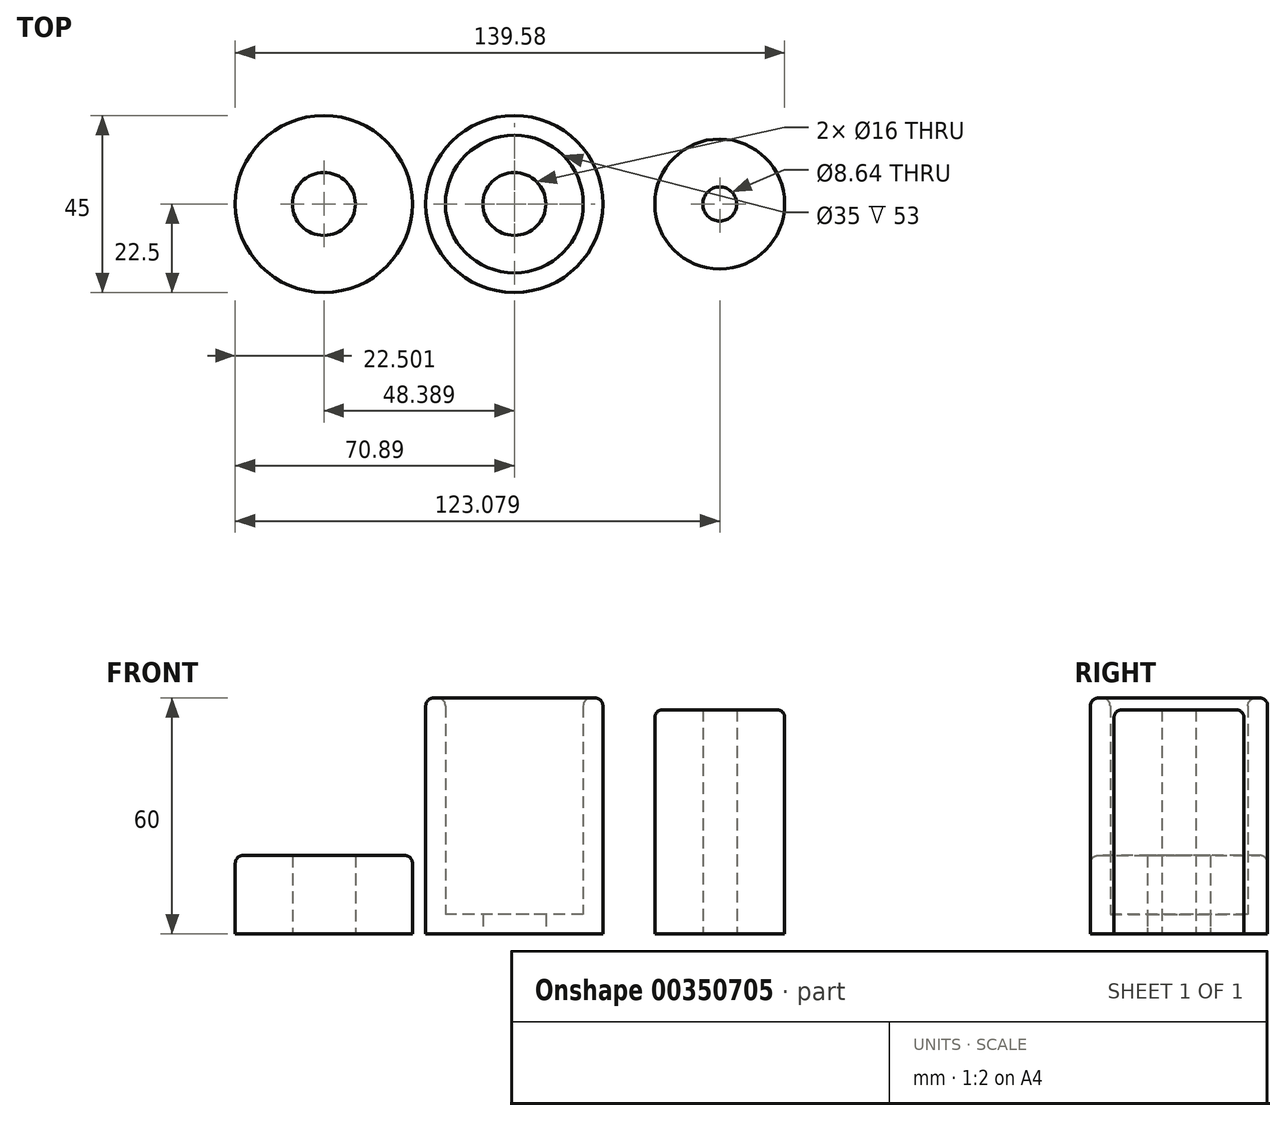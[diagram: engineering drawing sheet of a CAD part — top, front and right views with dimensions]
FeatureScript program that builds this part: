
annotation { "Feature Type Name" : "Feature", "Feature Type Description" : "" }
export const myFeature = defineFeature(function(context is Context, id is Id, definition is map)
    precondition{}
    {
        {
            var Q0;
            Q0=qCreatedBy(makeId("Top.planeOp"),FACE);
            var sketch = newSketch(context, id + "F0", { "sketchPlane" : qUnion([Q0])});
            skCircle(sketch, "E0", {"center": v(0, 0) * mm, "radius": 22.5 * mm});
            skSolve(sketch);
        }
        {
            var Q0;
            Q0 = qSketchRegion(id + "F0", true);
            extrude(context, id + "F1", {"entities" : qUnion([Q0]), "depth" : 60 * mm});
        }
        {
            var Q0;
            Q0=makeQuery(id+"F1.opExtrude","CAP_FACE",FACE,{"disambiguationData":[OSD([sQuery(id+"F0.wireOp",EDGE,"E0")])],"isStart":false});
            shell(context, id + "F2", {"entities" : qUnion([Q0]), "thickness" : 5 * mm});
        }
        {
            var Q0;
            Q0=qCreatedBy(makeId("Top.planeOp"),FACE);
            var sketch = newSketch(context, id + "F3", { "sketchPlane" : qUnion([Q0])});
            skCircle(sketch, "E1", {"center": v(52.19, 0) * mm, "radius": 16.5 * mm});
            skSolve(sketch);
        }
        {
            var Q0;
            Q0=makeQuery(id+"F3.imprint","IMPRINT",FACE,{"disambiguationData":[TD([[makeQuery(id+"F3.imprint","IMPRINT",EDGE,{"derivedFrom":sQuery(id+"F3.wireOp",EDGE,"E1")}),1.0]])]});
            extrude(context, id + "F4", {"entities" : qUnion([Q0]), "depth" : 57 * mm});
        }
        {
            var Q0;
            Q0=qCreatedBy(makeId("Top.planeOp"),FACE);
            var sketch = newSketch(context, id + "F5", { "sketchPlane" : qUnion([Q0])});
            skCircle(sketch, "E2", {"center": v(-48.39, 0) * mm, "radius": 22.5 * mm});
            skSolve(sketch);
        }
        {
            var Q0;
            Q0 = qSketchRegion(id + "F5", true);
            extrude(context, id + "F6", {"entities" : qUnion([Q0]), "depth" : 20 * mm});
        }
        {
            var Q0;
            Q0=makeQuery(id+"F4.opExtrude","CAP_EDGE",EDGE,{"disambiguationData":[OSD([sQuery(id+"F3.wireOp",EDGE,"E1")])],"isStart":false});
            var Q1;
            {var subQ0=sQuery(id+"F0.wireOp",EDGE,"E0");Q1=makeQuery(id+"F2.opShell","OFFSET_EDGE",EDGE,{"disambiguationData":[OSD([subQ0]),TDD([makeQuery(id+"F1.opExtrude","CAP_EDGE",EDGE,{"disambiguationData":[OSD([subQ0])],"isStart":false})])]});}
            var Q2;
            Q2=makeQuery(id+"F6.opExtrude","CAP_EDGE",EDGE,{"disambiguationData":[OSD([sQuery(id+"F5.wireOp",EDGE,"E2")])],"isStart":false});
            var Q3;
            Q3=makeQuery(id+"F1.opExtrude","CAP_EDGE",EDGE,{"disambiguationData":[OSD([sQuery(id+"F0.wireOp",EDGE,"E0")])],"isStart":false});
            fillet(context, id + "F7", {"entities" : qUnion([Q0, Q1, Q2, Q3]), "radius" : 2 * mm, "tangentPropagation" : true, "allowEdgeOverflow" : false});
        }
        {
            var Q0;
            Q0=qCreatedBy(makeId("Top.planeOp"),FACE);
            var sketch = newSketch(context, id + "F8", { "sketchPlane" : qUnion([Q0])});
            skCircle(sketch, "E3", {"center": v(-48.39, 0) * mm, "radius": 8 * mm});
            skCircle(sketch, "E4", {"center": v(52.19, 0) * mm, "radius": 4.32 * mm});
            skCircle(sketch, "E5", {"center": v(0, 0) * mm, "radius": 8 * mm});
            skSolve(sketch);
        }
        {
            var Q0;
            Q0 = qSketchRegion(id + "F8", true);
            extrude(context, id + "F9", {"entities" : qUnion([Q0]), "operationType" : NewBodyOperationType.REMOVE, "depth" : 104.9 * mm});
        }
    });
